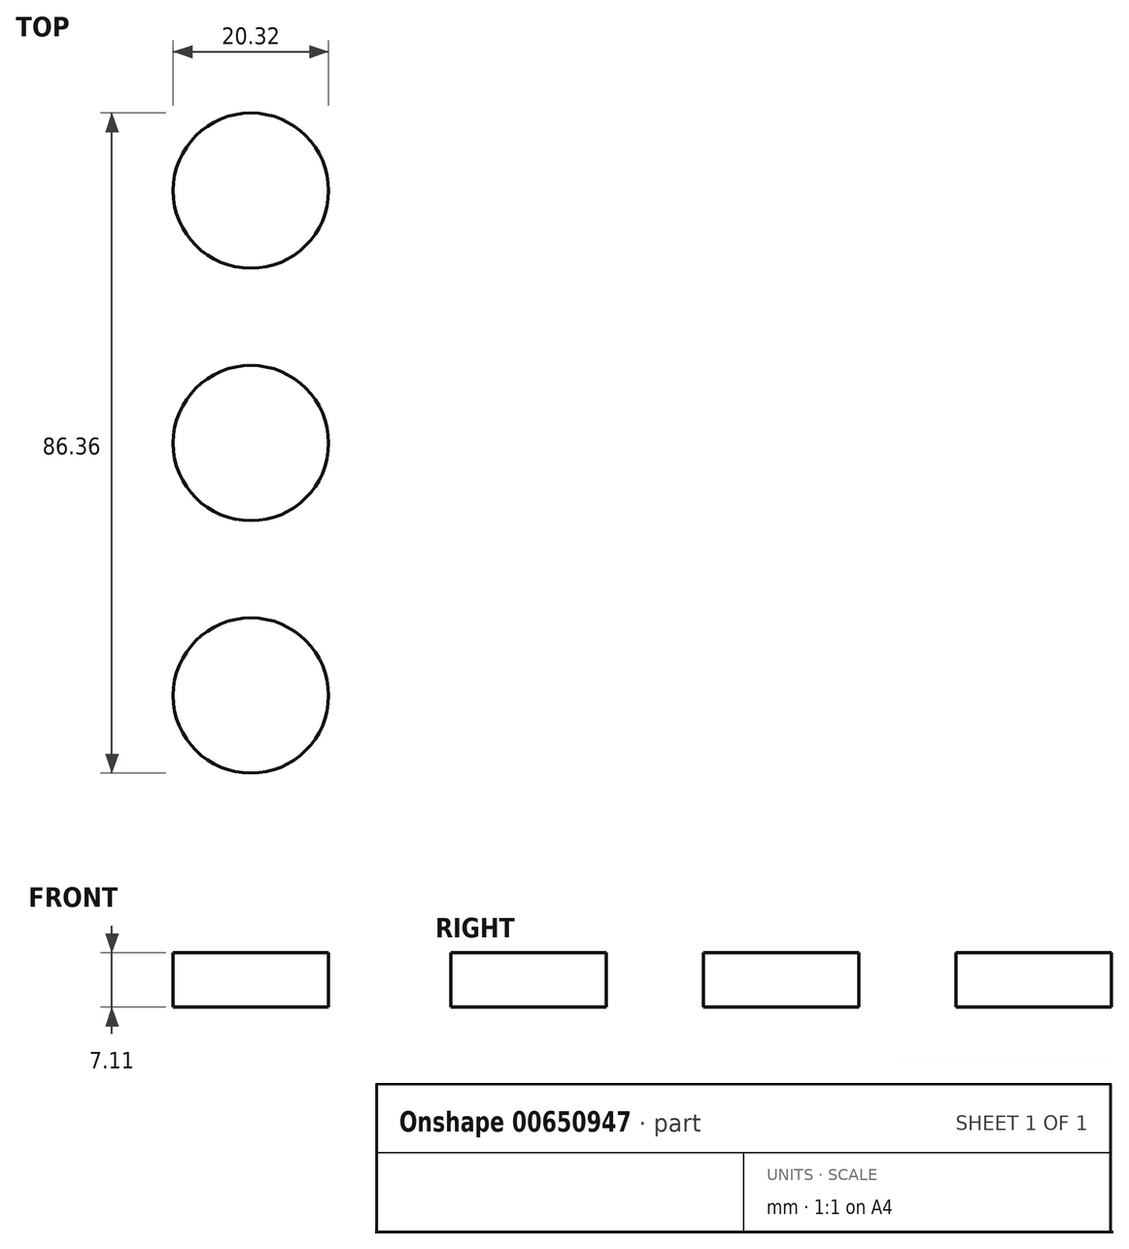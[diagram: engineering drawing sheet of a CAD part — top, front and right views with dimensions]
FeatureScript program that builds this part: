
annotation { "Feature Type Name" : "Feature", "Feature Type Description" : "" }
export const myFeature = defineFeature(function(context is Context, id is Id, definition is map)
    precondition{}
    {
        {
            var Q0;
            Q0=qCreatedBy(makeId("Top.planeOp"),FACE);
            var sketch = newSketch(context, id + "F0", { "sketchPlane" : qUnion([Q0])});
            skCircle(sketch, "E0", {"center": v(0, 33.02) * mm, "radius": 10.16 * mm});
            skCircle(sketch, "E1", {"center": v(0, -33.02) * mm, "radius": 10.16 * mm});
            skSolve(sketch);
        }
        {
            var Q0;
            Q0=qCreatedBy(makeId("Top.planeOp"),FACE);
            var sketch = newSketch(context, id + "F1", { "sketchPlane" : qUnion([Q0])});
            skCircle(sketch, "E2", {"center": v(0, 0) * mm, "radius": 10.16 * mm});
            skSolve(sketch);
        }
        {
            var Q0;
            Q0=makeQuery(id+"F0.imprint","IMPRINT",FACE,{"disambiguationData":[TD([[makeQuery(id+"F0.imprint","IMPRINT",EDGE,{"derivedFrom":sQuery(id+"F0.wireOp",EDGE,"E0")}),1.0]])]});
            var Q1;
            Q1=makeQuery(id+"F1.imprint","IMPRINT",FACE,{"disambiguationData":[TD([[makeQuery(id+"F1.imprint","IMPRINT",EDGE,{"derivedFrom":sQuery(id+"F1.wireOp",EDGE,"E2")}),1.0]])]});
            var Q2;
            Q2=makeQuery(id+"F0.imprint","IMPRINT",FACE,{"disambiguationData":[TD([[makeQuery(id+"F0.imprint","IMPRINT",EDGE,{"derivedFrom":sQuery(id+"F0.wireOp",EDGE,"E1")}),1.0]])]});
            extrude(context, id + "F2", {"entities" : qUnion([Q0, Q1, Q2]), "depth" : 7.11 * mm, "offsetDistance" : 25.4 * mm});
        }
    });
